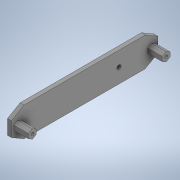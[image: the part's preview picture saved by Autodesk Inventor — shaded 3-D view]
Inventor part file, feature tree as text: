
AUTODESK INVENTOR PART (.ipt)
format: ipt  version: 2020 (Build 240168000, 168)  size: 250,368 bytes
history: native  units: in
note: dims shown in document units (in); Inventor stores cm internally (conversion verified against a paired STEP export)
features: extrude x6, sketch x6, plane x1
ambient origin geometry x8: Origin, YZ Plane, XZ Plane, XY Plane, X Axis, Y Axis, Z Axis, Center Point
bodies: Solid1 (feature_tree)
feature tree (13):
  extrude  "Extrusion1"  Depth=5.9055in
  extrude  "Extrusion3"  TaperAngle=0.0deg  [1 undecoded]
  extrude  "Extrusion4"  Depth=0.5906in
  plane  "Work Plane1"
  extrude  "Extrusion5"  Depth=0.122in
  extrude  "Extrusion6"  Depth=0.2402in
  extrude  "Extrusion7"  [1 undecoded]
  sketch  "Sketch1"  dims[d0=1.1811in d1=5.9055in]
  sketch  "Sketch2"  dims[d2=0.1575in d3=0.0in]
  sketch  "Sketch3"  dims[d8=0.315in d9=0.5906in]
  sketch  "Sketch4"  dims[d10=0.0in d12=0.122in]
  sketch  "Sketch5"  dims[d13=0.0in d14=0.0in d15=0.2402in]
  sketch  "Sketch8"  dims[d16=0.0866in d17=-0.2233in d18=-0.3937in d19=0.0866in d20=0.0in d26=1.5748in d27=0.1654in d30=0.0in d31=0.0in]
note: 2 required parameter values undecoded (feature->parameter linkage not recoverable at this tier; creation-order binding heuristic only, values carry confidence <= 0.55)
